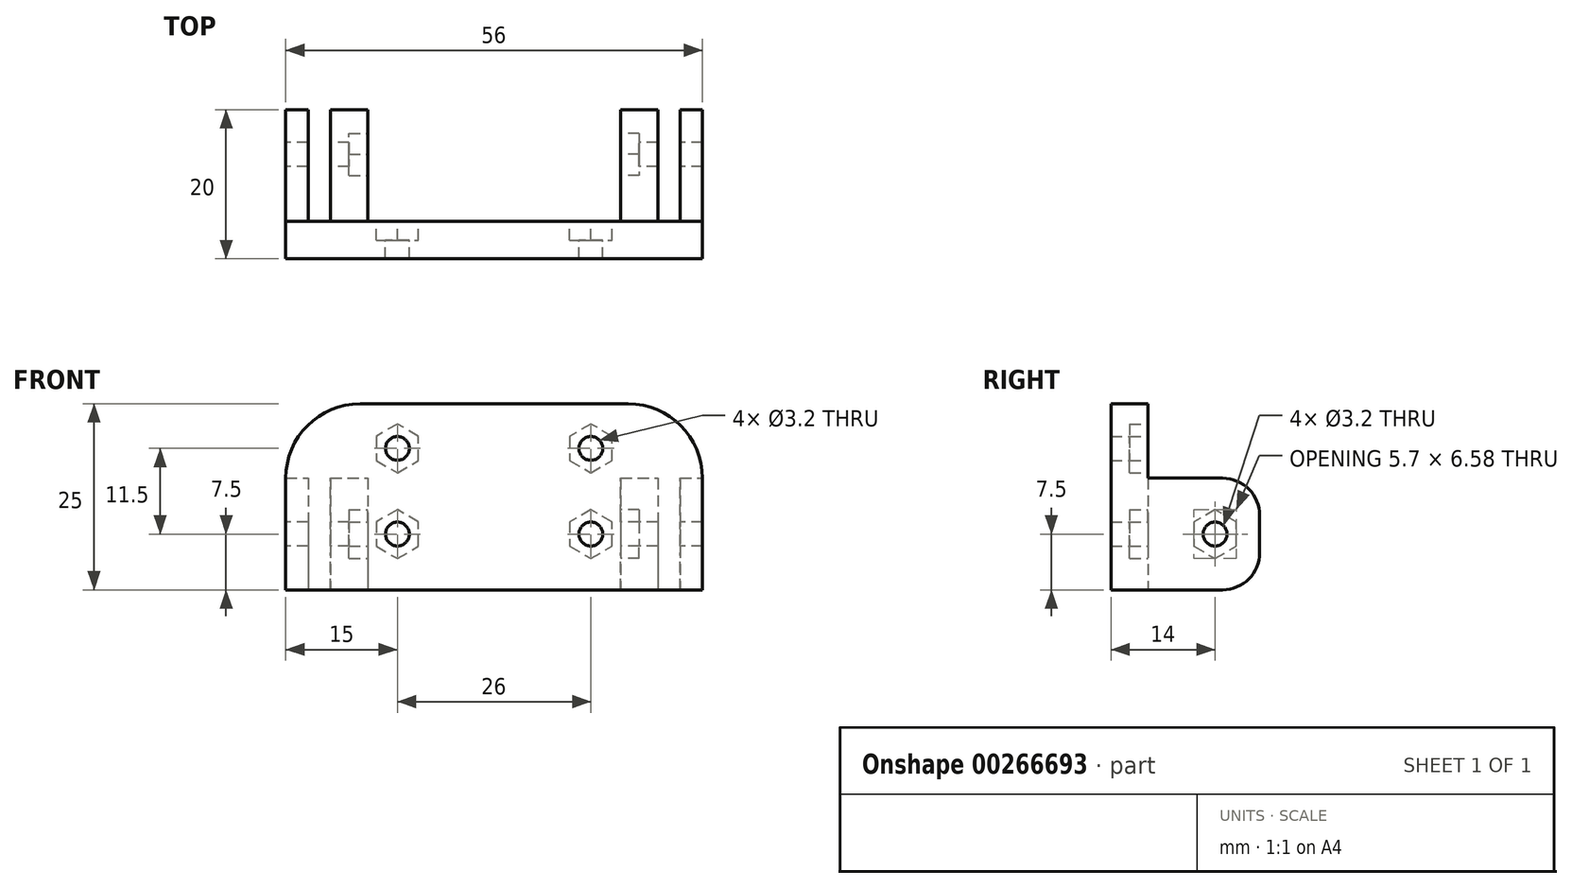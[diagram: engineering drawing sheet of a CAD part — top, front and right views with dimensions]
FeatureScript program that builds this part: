
annotation { "Feature Type Name" : "Feature", "Feature Type Description" : "" }
export const myFeature = defineFeature(function(context is Context, id is Id, definition is map)
    precondition{}
    {
        {
            var Q0;
            Q0=qCreatedBy(makeId("Top.planeOp"),FACE);
            var sketch = newSketch(context, id + "F0", { "sketchPlane" : qUnion([Q0])});
            skLineSegment(sketch, "E0", {"start": v(-28, 0) * mm, "end": v(28, 0) * mm});
            skLineSegment(sketch, "E1", {"start": v(28, 20) * mm, "end": v(25, 20) * mm});
            skLineSegment(sketch, "E2", {"start": v(25, 20) * mm, "end": v(25, 5) * mm});
            skLineSegment(sketch, "E3", {"start": v(25, 5) * mm, "end": v(22, 5) * mm});
            skLineSegment(sketch, "E4", {"start": v(22, 5) * mm, "end": v(22, 20) * mm});
            skLineSegment(sketch, "E5", {"start": v(22, 20) * mm, "end": v(17, 20) * mm});
            skLineSegment(sketch, "E6", {"start": v(17, 20) * mm, "end": v(17, 5) * mm});
            skLineSegment(sketch, "E7", {"start": v(17, 5) * mm, "end": v(-17, 5) * mm});
            skLineSegment(sketch, "E8", {"start": v(-17, 5) * mm, "end": v(-17, 20) * mm});
            skLineSegment(sketch, "E9", {"start": v(-17, 20) * mm, "end": v(-22, 20) * mm});
            skLineSegment(sketch, "E10", {"start": v(-22, 20) * mm, "end": v(-22, 5) * mm});
            skLineSegment(sketch, "E11", {"start": v(-22, 5) * mm, "end": v(-25, 5) * mm});
            skLineSegment(sketch, "E12", {"start": v(-25, 5) * mm, "end": v(-25, 20) * mm});
            skLineSegment(sketch, "E13", {"start": v(-25, 20) * mm, "end": v(-28, 20) * mm});
            skLineSegment(sketch, "E14", {"start": v(-28, 20) * mm, "end": v(-28, 0) * mm});
            skLineSegment(sketch, "E15", {"start": v(28, 20) * mm, "end": v(28, 0) * mm});
            skSolve(sketch);
        }
        {
            var Q0;
            Q0 = qSketchRegion(id + "F0", true);
            extrude(context, id + "F1", {"entities" : qUnion([Q0]), "depth" : 15 * mm});
        }
        {
            var Q0;
            Q0=makeQuery(id+"F1.opExtrude","SWEPT_FACE",FACE,{"disambiguationData":[OSD([sQuery(id+"F0.wireOp",EDGE,"E14")])]});
            var sketch = newSketch(context, id + "F2", { "sketchPlane" : qUnion([Q0])});
            skCircle(sketch, "E16", {"center": v(-14, 7.5) * mm, "radius": 1.6 * mm});
            skPoint(sketch, "E16.centerSnap0", {"position": v(0, 7.5) * mm});
            skSolve(sketch);
        }
        {
            var Q0;
            Q0 = qSketchRegion(id + "F2", true);
            extrude(context, id + "F3", {"entities" : qUnion([Q0]), "operationType" : NewBodyOperationType.REMOVE, "endBound" : BoundingType.THROUGH_ALL, "oppositeDirection" : true, "depth" : 25 * mm});
        }
        {
            var Q0;
            Q0=makeQuery(id+"F1.opExtrude","SWEPT_FACE",FACE,{"disambiguationData":[OSD([sQuery(id+"F0.wireOp",EDGE,"E8")])]});
            var sketch = newSketch(context, id + "F4", { "sketchPlane" : qUnion([Q0])});
            skCircle(sketch, "E17.cCircle", {"center": v(14, 7.5) * mm, "radius": 2.85 * mm, "construction": true});
            skLineSegment(sketch, "E17.0", {"start": v(16.85, 9.15) * mm, "end": v(16.85, 5.85) * mm});
            skLineSegment(sketch, "E17.1", {"start": v(16.85, 5.85) * mm, "end": v(14, 4.2) * mm});
            skLineSegment(sketch, "E17.2", {"start": v(14, 4.2) * mm, "end": v(11.15, 5.85) * mm});
            skLineSegment(sketch, "E17.3", {"start": v(11.15, 5.85) * mm, "end": v(11.15, 9.15) * mm});
            skLineSegment(sketch, "E17.4", {"start": v(11.15, 9.15) * mm, "end": v(14, 10.8) * mm});
            skLineSegment(sketch, "E17.5", {"start": v(14, 10.8) * mm, "end": v(16.85, 9.15) * mm});
            skPoint(sketch, "E17.0.midPoint", {"position": v(16.85, 7.5) * mm});
            skSolve(sketch);
        }
        {
            var Q0;
            Q0 = qSketchRegion(id + "F4", true);
            extrude(context, id + "F5", {"entities" : qUnion([Q0]), "operationType" : NewBodyOperationType.REMOVE, "oppositeDirection" : true, "depth" : 2.5 * mm});
        }
        {
            var Q0;
            Q0=makeQuery(id+"F1.opExtrude","SWEPT_FACE",FACE,{"disambiguationData":[OSD([sQuery(id+"F0.wireOp",EDGE,"E6")])]});
            var sketch = newSketch(context, id + "F6", { "sketchPlane" : qUnion([Q0])});
            skCircle(sketch, "E18.cCircle", {"center": v(-14, 7.5) * mm, "radius": 2.85 * mm, "construction": true});
            skLineSegment(sketch, "E18.0", {"start": v(-11.15, 9.15) * mm, "end": v(-11.15, 5.85) * mm});
            skLineSegment(sketch, "E18.1", {"start": v(-11.15, 5.85) * mm, "end": v(-14, 4.2) * mm});
            skLineSegment(sketch, "E18.2", {"start": v(-14, 4.2) * mm, "end": v(-16.85, 5.85) * mm});
            skLineSegment(sketch, "E18.3", {"start": v(-16.85, 5.85) * mm, "end": v(-16.85, 9.15) * mm});
            skLineSegment(sketch, "E18.4", {"start": v(-16.85, 9.15) * mm, "end": v(-14, 10.8) * mm});
            skLineSegment(sketch, "E18.5", {"start": v(-14, 10.8) * mm, "end": v(-11.15, 9.15) * mm});
            skPoint(sketch, "E18.0.midPoint", {"position": v(-11.15, 7.5) * mm});
            skSolve(sketch);
        }
        {
            var Q0;
            Q0 = qSketchRegion(id + "F6", true);
            extrude(context, id + "F7", {"entities" : qUnion([Q0]), "operationType" : NewBodyOperationType.REMOVE, "oppositeDirection" : true, "depth" : 2.5 * mm});
        }
        {
            var Q0;
            Q0=makeQuery(id+"F1.opExtrude","CAP_FACE",FACE,{"disambiguationData":[OSD([sQuery(id+"F0.wireOp",EDGE,"E0"),sQuery(id+"F0.wireOp",EDGE,"E1"),sQuery(id+"F0.wireOp",EDGE,"E2"),sQuery(id+"F0.wireOp",EDGE,"E3"),sQuery(id+"F0.wireOp",EDGE,"E4"),sQuery(id+"F0.wireOp",EDGE,"E5"),sQuery(id+"F0.wireOp",EDGE,"E6"),sQuery(id+"F0.wireOp",EDGE,"E7"),sQuery(id+"F0.wireOp",EDGE,"E8"),sQuery(id+"F0.wireOp",EDGE,"E9"),sQuery(id+"F0.wireOp",EDGE,"E10"),sQuery(id+"F0.wireOp",EDGE,"E11"),sQuery(id+"F0.wireOp",EDGE,"E12"),sQuery(id+"F0.wireOp",EDGE,"E13"),sQuery(id+"F0.wireOp",EDGE,"E14"),sQuery(id+"F0.wireOp",EDGE,"E15")])],"isStart":false});
            var sketch = newSketch(context, id + "F8", { "sketchPlane" : qUnion([Q0])});
            skLineSegment(sketch, "E19.bottom", {"start": v(-28, 0) * mm, "end": v(28, 0) * mm});
            skLineSegment(sketch, "E19.top", {"start": v(-28, 5) * mm, "end": v(28, 5) * mm});
            skLineSegment(sketch, "E19.left", {"start": v(-28, 0) * mm, "end": v(-28, 5) * mm});
            skLineSegment(sketch, "E19.right", {"start": v(28, 0) * mm, "end": v(28, 5) * mm});
            skSolve(sketch);
        }
        {
            var Q0;
            Q0 = qSketchRegion(id + "F8", true);
            extrude(context, id + "F9", {"entities" : qUnion([Q0]), "operationType" : NewBodyOperationType.ADD, "depth" : 10 * mm});
        }
        {
            var Q0;
            Q0=makeQuery(id+"F1.opExtrude","SWEPT_FACE",FACE,{"disambiguationData":[OSD([sQuery(id+"F0.wireOp",EDGE,"E7")])]});
            var sketch = newSketch(context, id + "F10", { "sketchPlane" : qUnion([Q0])});
            skLineSegment(sketch, "E20", {"start": v(-13, 7.5) * mm, "end": v(13, 7.5) * mm, "construction": true});
            skPoint(sketch, "E21", {"position": v(0, 7.5) * mm});
            skCircle(sketch, "E22", {"center": v(-13, 7.5) * mm, "radius": 1.6 * mm});
            skCircle(sketch, "E23", {"center": v(13, 7.5) * mm, "radius": 1.6 * mm});
            skLineSegment(sketch, "E24", {"start": v(-13, 19) * mm, "end": v(13, 19) * mm, "construction": true});
            skPoint(sketch, "E25", {"position": v(0, 19) * mm});
            skCircle(sketch, "E26", {"center": v(-13, 19) * mm, "radius": 1.6 * mm});
            skCircle(sketch, "E27", {"center": v(13, 19) * mm, "radius": 1.6 * mm});
            skSolve(sketch);
        }
        {
            var Q0;
            Q0 = qSketchRegion(id + "F10", true);
            extrude(context, id + "F11", {"entities" : qUnion([Q0]), "operationType" : NewBodyOperationType.REMOVE, "endBound" : BoundingType.THROUGH_ALL, "oppositeDirection" : true, "depth" : 25 * mm});
        }
        {
            var Q0;
            Q0=makeQuery(id+"F1.opExtrude","SWEPT_FACE",FACE,{"disambiguationData":[OSD([sQuery(id+"F0.wireOp",EDGE,"E7")])]});
            var sketch = newSketch(context, id + "F12", { "sketchPlane" : qUnion([Q0])});
            skCircle(sketch, "E28.cCircle", {"center": v(-13, 7.5) * mm, "radius": 2.85 * mm, "construction": true});
            skLineSegment(sketch, "E28.0", {"start": v(-10.15, 9.15) * mm, "end": v(-10.15, 5.85) * mm});
            skLineSegment(sketch, "E28.1", {"start": v(-10.15, 5.85) * mm, "end": v(-13, 4.2) * mm});
            skLineSegment(sketch, "E28.2", {"start": v(-13, 4.2) * mm, "end": v(-15.85, 5.85) * mm});
            skLineSegment(sketch, "E28.3", {"start": v(-15.85, 5.85) * mm, "end": v(-15.85, 9.15) * mm});
            skLineSegment(sketch, "E28.4", {"start": v(-15.85, 9.15) * mm, "end": v(-13, 10.8) * mm});
            skLineSegment(sketch, "E28.5", {"start": v(-13, 10.8) * mm, "end": v(-10.15, 9.15) * mm});
            skPoint(sketch, "E28.0.midPoint", {"position": v(-10.15, 7.5) * mm});
            skCircle(sketch, "E29.cCircle", {"center": v(13, 7.5) * mm, "radius": 2.85 * mm, "construction": true});
            skLineSegment(sketch, "E29.0", {"start": v(10.15, 5.85) * mm, "end": v(10.15, 9.15) * mm});
            skLineSegment(sketch, "E29.1", {"start": v(10.15, 9.15) * mm, "end": v(13, 10.8) * mm});
            skLineSegment(sketch, "E29.2", {"start": v(13, 10.8) * mm, "end": v(15.85, 9.15) * mm});
            skLineSegment(sketch, "E29.3", {"start": v(15.85, 9.15) * mm, "end": v(15.85, 5.85) * mm});
            skLineSegment(sketch, "E29.4", {"start": v(15.85, 5.85) * mm, "end": v(13, 4.2) * mm});
            skLineSegment(sketch, "E29.5", {"start": v(13, 4.2) * mm, "end": v(10.15, 5.85) * mm});
            skPoint(sketch, "E29.0.midPoint", {"position": v(10.15, 7.5) * mm});
            skCircle(sketch, "E30.cCircle", {"center": v(-13, 19) * mm, "radius": 2.85 * mm, "construction": true});
            skLineSegment(sketch, "E30.0", {"start": v(-15.85, 17.35) * mm, "end": v(-15.85, 20.65) * mm});
            skLineSegment(sketch, "E30.1", {"start": v(-15.85, 20.65) * mm, "end": v(-13, 22.3) * mm});
            skLineSegment(sketch, "E30.2", {"start": v(-13, 22.3) * mm, "end": v(-10.15, 20.65) * mm});
            skLineSegment(sketch, "E30.3", {"start": v(-10.15, 20.65) * mm, "end": v(-10.15, 17.35) * mm});
            skLineSegment(sketch, "E30.4", {"start": v(-10.15, 17.35) * mm, "end": v(-13, 15.7) * mm});
            skLineSegment(sketch, "E30.5", {"start": v(-13, 15.7) * mm, "end": v(-15.85, 17.35) * mm});
            skPoint(sketch, "E30.0.midPoint", {"position": v(-15.85, 19) * mm});
            skCircle(sketch, "E31.cCircle", {"center": v(13, 19) * mm, "radius": 2.85 * mm, "construction": true});
            skLineSegment(sketch, "E31.0", {"start": v(15.85, 20.65) * mm, "end": v(15.85, 17.35) * mm});
            skLineSegment(sketch, "E31.1", {"start": v(15.85, 17.35) * mm, "end": v(13, 15.7) * mm});
            skLineSegment(sketch, "E31.2", {"start": v(13, 15.7) * mm, "end": v(10.15, 17.35) * mm});
            skLineSegment(sketch, "E31.3", {"start": v(10.15, 17.35) * mm, "end": v(10.15, 20.65) * mm});
            skLineSegment(sketch, "E31.4", {"start": v(10.15, 20.65) * mm, "end": v(13, 22.3) * mm});
            skLineSegment(sketch, "E31.5", {"start": v(13, 22.3) * mm, "end": v(15.85, 20.65) * mm});
            skPoint(sketch, "E31.0.midPoint", {"position": v(15.85, 19) * mm});
            skSolve(sketch);
        }
        {
            var Q0;
            Q0 = qSketchRegion(id + "F12", true);
            extrude(context, id + "F13", {"entities" : qUnion([Q0]), "operationType" : NewBodyOperationType.REMOVE, "oppositeDirection" : true, "depth" : 2.5 * mm});
        }
        {
            var Q0;
            Q0=makeQuery(id+"F9.opExtrude","CAP_EDGE",EDGE,{"disambiguationData":[OSD([sQuery(id+"F8.wireOp",EDGE,"E19.right")])],"isStart":false});
            var Q1;
            Q1=makeQuery(id+"F9.opExtrude","CAP_EDGE",EDGE,{"disambiguationData":[OSD([sQuery(id+"F8.wireOp",EDGE,"E19.left")])],"isStart":false});
            fillet(context, id + "F14", {"entities" : qUnion([Q0, Q1]), "radius" : 10 * mm, "tangentPropagation" : true, "allowEdgeOverflow" : false});
        }
        {
            var Q0;
            Q0=makeQuery(id+"F1.opExtrude","CAP_EDGE",EDGE,{"disambiguationData":[OSD([sQuery(id+"F0.wireOp",EDGE,"E1")])],"isStart":false});
            var Q1;
            Q1=makeQuery(id+"F1.opExtrude","CAP_EDGE",EDGE,{"disambiguationData":[OSD([sQuery(id+"F0.wireOp",EDGE,"E5")])],"isStart":false});
            var Q2;
            Q2=makeQuery(id+"F1.opExtrude","CAP_EDGE",EDGE,{"disambiguationData":[OSD([sQuery(id+"F0.wireOp",EDGE,"E1")])],"isStart":true});
            var Q3;
            Q3=makeQuery(id+"F1.opExtrude","CAP_EDGE",EDGE,{"disambiguationData":[OSD([sQuery(id+"F0.wireOp",EDGE,"E5")])],"isStart":true});
            var Q4;
            Q4=makeQuery(id+"F1.opExtrude","CAP_EDGE",EDGE,{"disambiguationData":[OSD([sQuery(id+"F0.wireOp",EDGE,"E9")])],"isStart":true});
            var Q5;
            Q5=makeQuery(id+"F1.opExtrude","CAP_EDGE",EDGE,{"disambiguationData":[OSD([sQuery(id+"F0.wireOp",EDGE,"E13")])],"isStart":true});
            var Q6;
            Q6=makeQuery(id+"F1.opExtrude","CAP_EDGE",EDGE,{"disambiguationData":[OSD([sQuery(id+"F0.wireOp",EDGE,"E13")])],"isStart":false});
            var Q7;
            Q7=makeQuery(id+"F1.opExtrude","CAP_EDGE",EDGE,{"disambiguationData":[OSD([sQuery(id+"F0.wireOp",EDGE,"E9")])],"isStart":false});
            fillet(context, id + "F15", {"entities" : qUnion([Q0, Q1, Q2, Q3, Q4, Q5, Q6, Q7]), "radius" : 5 * mm, "tangentPropagation" : true, "allowEdgeOverflow" : false});
        }
    });
